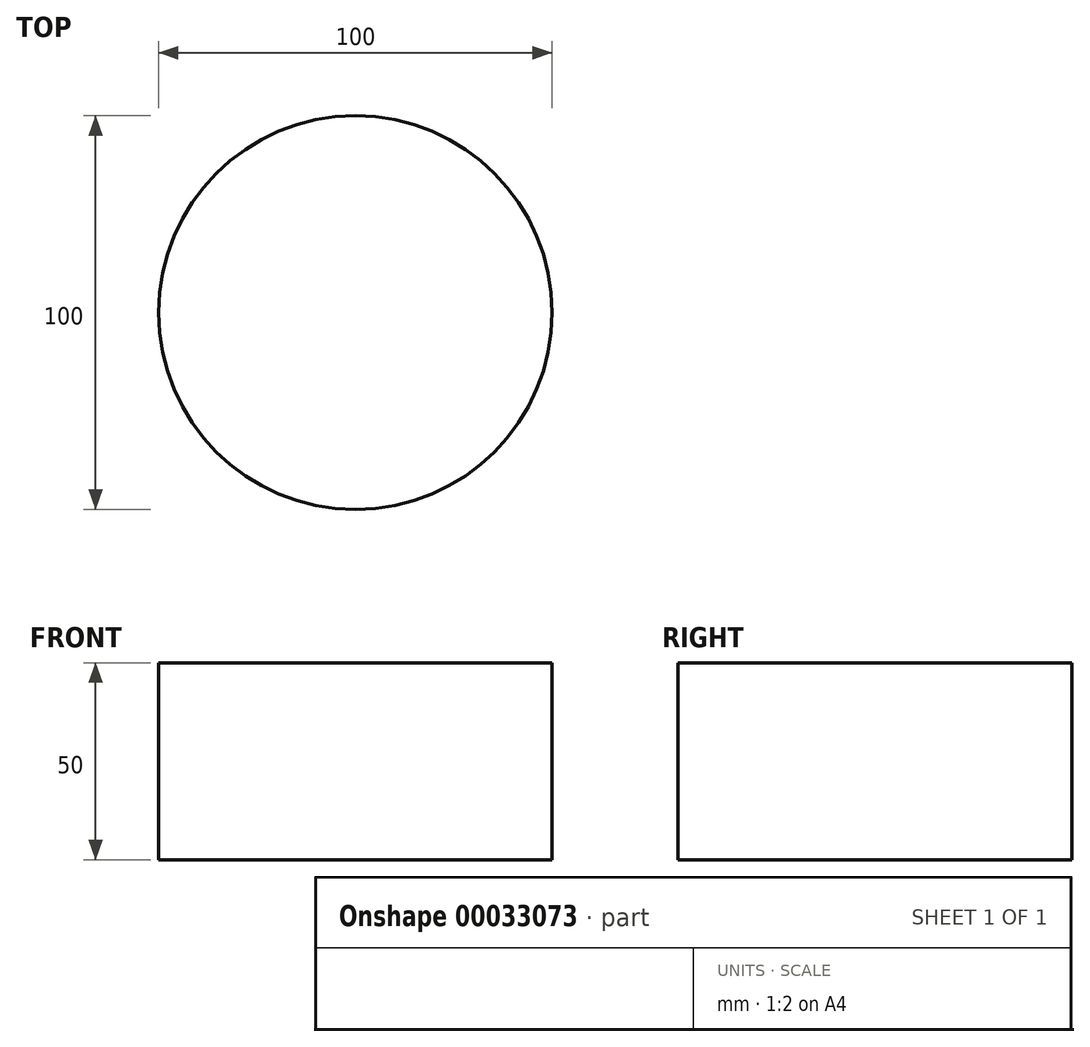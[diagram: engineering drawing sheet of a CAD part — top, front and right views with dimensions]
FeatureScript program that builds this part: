
annotation { "Feature Type Name" : "Feature", "Feature Type Description" : "" }
export const myFeature = defineFeature(function(context is Context, id is Id, definition is map)
    precondition{}
    {
        {
            var Q0;
            Q0=qCreatedBy(makeId("Top.planeOp"),FACE);
            var sketch = newSketch(context, id + "F0", { "sketchPlane" : qUnion([Q0])});
            skCircle(sketch, "E0", {"center": v(0, 0) * mm, "radius": 50 * mm});
            skSolve(sketch);
        }
        {
            var Q0;
            Q0 = qSketchRegion(id + "F0", true);
            extrude(context, id + "F1", {"entities" : qUnion([Q0]), "endBound" : BoundingType.SYMMETRIC, "depth" : 50 * mm});
        }
    });
